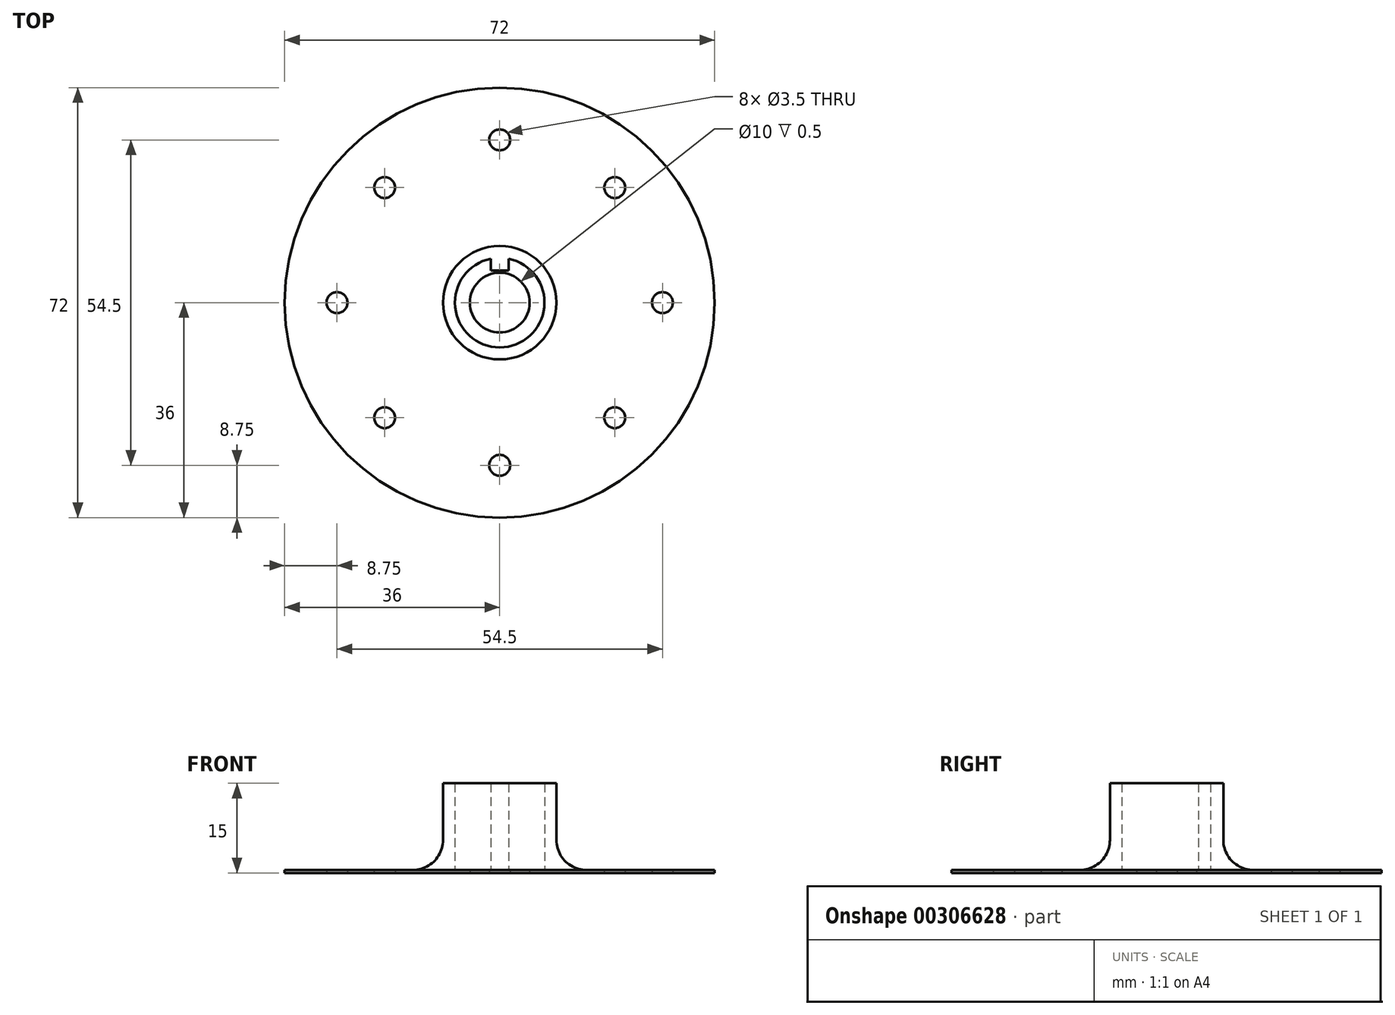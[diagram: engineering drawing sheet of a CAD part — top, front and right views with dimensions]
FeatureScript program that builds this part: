
annotation { "Feature Type Name" : "Feature", "Feature Type Description" : "" }
export const myFeature = defineFeature(function(context is Context, id is Id, definition is map)
    precondition{}
    {
        {
            assignVariable(context, id + "F0", {"name" : "Thicc", "anyValue" : .5});
        }
        {
            var Q0;
            Q0=qCreatedBy(makeId("Top.planeOp"),FACE);
            var sketch = newSketch(context, id + "F1", { "sketchPlane" : qUnion([Q0])});
            skCircle(sketch, "E0", {"center": v(0, 0) * mm, "radius": 7.5 * mm});
            skCircle(sketch, "E1", {"center": v(0, 0) * mm, "radius": 9.5 * mm});
            skLineSegment(sketch, "E2", {"start": v(-1.5, 7.35) * mm, "end": v(-1.5, 5.35) * mm});
            skLineSegment(sketch, "E3", {"start": v(-1.5, 5.35) * mm, "end": v(1.5, 5.35) * mm});
            skLineSegment(sketch, "E4", {"start": v(1.5, 5.35) * mm, "end": v(1.5, 7.35) * mm});
            skPoint(sketch, "E5", {"position": v(0, 5.35) * mm});
            skSolve(sketch);
        }
        {
            var Q0;
            Q0=qCreatedBy(makeId("Top.planeOp"),FACE);
            var sketch = newSketch(context, id + "F2", { "sketchPlane" : qUnion([Q0])});
            skCircle(sketch, "E6", {"center": v(0, 0) * mm, "radius": 2.5 * mm});
            skCircle(sketch, "E7", {"center": v(0, 0) * mm, "radius": 27.25 * mm});
            skCircle(sketch, "E8", {"center": v(0, 0) * mm, "radius": 6 * mm});
            skCircle(sketch, "E9", {"center": v(0, 0) * mm, "radius": 36 * mm});
            skPoint(sketch, "E10", {"position": v(-6, 0) * mm});
            skPoint(sketch, "E11", {"position": v(0, 6) * mm});
            skPoint(sketch, "E12", {"position": v(6, 0) * mm});
            skPoint(sketch, "E13", {"position": v(0, -6) * mm});
            skCircle(sketch, "E14", {"center": v(0, 0) * mm, "radius": 4 * mm, "construction": true});
            skCircle(sketch, "E15", {"center": v(0, 27.25) * mm, "radius": 1.75 * mm});
            skCircle(sketch, "E16.1.0", {"center": v(-19.27, 19.27) * mm, "radius": 1.75 * mm});
            skCircle(sketch, "E16.2.0", {"center": v(-27.25, 0) * mm, "radius": 1.75 * mm});
            skCircle(sketch, "E16.3.0", {"center": v(-19.27, -19.27) * mm, "radius": 1.75 * mm});
            skCircle(sketch, "E16.4.0", {"center": v(0, -27.25) * mm, "radius": 1.75 * mm});
            skCircle(sketch, "E16.5.0", {"center": v(19.27, -19.27) * mm, "radius": 1.75 * mm});
            skCircle(sketch, "E16.6.0", {"center": v(27.25, 0) * mm, "radius": 1.75 * mm});
            skCircle(sketch, "E16.7.0", {"center": v(19.27, 19.27) * mm, "radius": 1.75 * mm});
            skSolve(sketch);
        }
        {
            var Q0;
            Q0=makeQuery(id+"F2.imprint","IMPRINT",FACE,{"disambiguationData":[TD([[makeQuery(id+"F2.imprint","IMPRINT",EDGE,{"derivedFrom":sQuery(id+"F2.wireOp",EDGE,"E9")}),1.0]])]});
            var Q1;
            {var subQ9=sQuery(id+"F2.wireOp",EDGE,"dmMNSs5U-dXkE-OnuB-x4GF-gnbwgTEUMQlt");Q1=makeQuery(id+"F2.imprint","IMPRINT",FACE,{"disambiguationData":[TD([[makeQuery(id+"F2.imprint","IMPRINT",EDGE,{"derivedFrom":subQ9}),-1.0]])]});}
            var Q2;
            Q2=makeQuery(id+"F2.imprint","IMPRINT",FACE,{"disambiguationData":[TD([[makeQuery(id+"F2.imprint","IMPRINT",EDGE,{"derivedFrom":sQuery(id+"F2.wireOp",EDGE,"E6")}),-1.0]])]});
            var Q3;
            Q3=makeQuery(id+"F2.imprint","IMPRINT",FACE,{"disambiguationData":[TD([[makeQuery(id+"F2.imprint","IMPRINT",EDGE,{"derivedFrom":sQuery(id+"F2.wireOp",EDGE,"IWH39UaP-91kU-eHGR-F86Z-JhOdxDluEBEP")}),1.0]])]});
            var Q4;
            Q4=makeQuery(id+"F2.imprint","IMPRINT",FACE,{"disambiguationData":[TD([[makeQuery(id+"F2.imprint","IMPRINT",EDGE,{"derivedFrom":sQuery(id+"F2.wireOp",EDGE,"xcFHTZrV-l3IJ-FcGW-Rsgo-3uNkYJn71cBD")}),1.0]])]});
            var Q5;
            Q5=makeQuery(id+"F2.imprint","IMPRINT",FACE,{"disambiguationData":[TD([[makeQuery(id+"F2.imprint","IMPRINT",EDGE,{"derivedFrom":sQuery(id+"F2.wireOp",EDGE,"dmMNSs5U-dXkE-OnuB-x4GF-gnbwgTEUMQlt")}),1.0]])]});
            var Q6;
            Q6=makeQuery(id+"F2.imprint","IMPRINT",FACE,{"disambiguationData":[TD([[makeQuery(id+"F2.imprint","IMPRINT",EDGE,{"derivedFrom":sQuery(id+"F2.wireOp",EDGE,"OsnEyq0h-FFfx-xI0f-fycZ-s3bM1W6ctmpb")}),1.0]])]});
            var Q7;
            {var subQ0=sQuery(id+"F2.wireOp",EDGE,"W7DDKYX3-tOsd-kb3P-etkb-bdxIaiogGMYC");var subQ1=sQuery(id+"F2.wireOp",EDGE,"E7");var subQ2=makeQuery(id+"F2.imprint","INTERSECT",VERTEX,{"disambiguationData":[OD(0.0)],"derivedFrom":[subQ1,subQ0]});Q7=makeQuery(id+"F2.imprint","IMPRINT",FACE,{"disambiguationData":[TD([[makeQuery(id+"F2.imprint","IMPRINT",EDGE,{"disambiguationData":[TD([[subQ2,-1.0]])],"derivedFrom":subQ1}),-1.0]])]});}
            var Q8;
            {var subQ0=sQuery(id+"F2.wireOp",EDGE,"W7DDKYX3-tOsd-kb3P-etkb-bdxIaiogGMYC");var subQ1=sQuery(id+"F2.wireOp",EDGE,"E7");var subQ2=makeQuery(id+"F2.imprint","INTERSECT",VERTEX,{"disambiguationData":[OD(0.0)],"derivedFrom":[subQ1,subQ0]});Q8=makeQuery(id+"F2.imprint","IMPRINT",FACE,{"disambiguationData":[TD([[makeQuery(id+"F2.imprint","IMPRINT",EDGE,{"disambiguationData":[TD([[subQ2,-1.0]])],"derivedFrom":subQ1}),1.0]])]});}
            var Q9;
            {var subQ0=sQuery(id+"F2.wireOp",EDGE,"AhLqCoLq-dUsO-Cpqc-C8LF-fpEpIzBaevSX");var subQ1=sQuery(id+"F2.wireOp",EDGE,"E7");var subQ2=makeQuery(id+"F2.imprint","INTERSECT",VERTEX,{"disambiguationData":[OD(0.0)],"derivedFrom":[subQ1,subQ0]});Q9=makeQuery(id+"F2.imprint","IMPRINT",FACE,{"disambiguationData":[TD([[makeQuery(id+"F2.imprint","IMPRINT",EDGE,{"disambiguationData":[TD([[subQ2,-1.0]])],"derivedFrom":subQ1}),-1.0]])]});}
            var Q10;
            {var subQ0=sQuery(id+"F2.wireOp",EDGE,"AhLqCoLq-dUsO-Cpqc-C8LF-fpEpIzBaevSX");var subQ1=sQuery(id+"F2.wireOp",EDGE,"E7");var subQ2=makeQuery(id+"F2.imprint","INTERSECT",VERTEX,{"disambiguationData":[OD(0.0)],"derivedFrom":[subQ1,subQ0]});Q10=makeQuery(id+"F2.imprint","IMPRINT",FACE,{"disambiguationData":[TD([[makeQuery(id+"F2.imprint","IMPRINT",EDGE,{"disambiguationData":[TD([[subQ2,-1.0]])],"derivedFrom":subQ1}),1.0]])]});}
            var Q11;
            {var subQ0=sQuery(id+"F2.wireOp",EDGE,"NGUcrRit-ETaF-dVqX-X14s-6RHGiHHLhfyM");var subQ1=sQuery(id+"F2.wireOp",EDGE,"E7");var subQ2=makeQuery(id+"F2.imprint","INTERSECT",VERTEX,{"disambiguationData":[OD(0.0)],"derivedFrom":[subQ1,subQ0]});Q11=makeQuery(id+"F2.imprint","IMPRINT",FACE,{"disambiguationData":[TD([[makeQuery(id+"F2.imprint","IMPRINT",EDGE,{"disambiguationData":[TD([[subQ2,-1.0]])],"derivedFrom":subQ1}),1.0]])]});}
            var Q12;
            {var subQ0=sQuery(id+"F2.wireOp",EDGE,"NGUcrRit-ETaF-dVqX-X14s-6RHGiHHLhfyM");var subQ1=sQuery(id+"F2.wireOp",EDGE,"E7");var subQ2=makeQuery(id+"F2.imprint","INTERSECT",VERTEX,{"disambiguationData":[OD(0.0)],"derivedFrom":[subQ1,subQ0]});Q12=makeQuery(id+"F2.imprint","IMPRINT",FACE,{"disambiguationData":[TD([[makeQuery(id+"F2.imprint","IMPRINT",EDGE,{"disambiguationData":[TD([[subQ2,-1.0]])],"derivedFrom":subQ1}),-1.0]])]});}
            var Q13;
            {var subQ0=sQuery(id+"F2.wireOp",EDGE,"sCoCbA2o-mAqV-ztxx-V3PG-5PHjPGKNcyER");var subQ1=sQuery(id+"F2.wireOp",EDGE,"E7");var subQ2=makeQuery(id+"F2.imprint","INTERSECT",VERTEX,{"disambiguationData":[OD(0.0)],"derivedFrom":[subQ1,subQ0]});Q13=makeQuery(id+"F2.imprint","IMPRINT",FACE,{"disambiguationData":[TD([[makeQuery(id+"F2.imprint","IMPRINT",EDGE,{"disambiguationData":[TD([[subQ2,-1.0]])],"derivedFrom":subQ1}),-1.0]])]});}
            var Q14;
            {var subQ0=sQuery(id+"F2.wireOp",EDGE,"sCoCbA2o-mAqV-ztxx-V3PG-5PHjPGKNcyER");var subQ1=sQuery(id+"F2.wireOp",EDGE,"E7");var subQ2=makeQuery(id+"F2.imprint","INTERSECT",VERTEX,{"disambiguationData":[OD(0.0)],"derivedFrom":[subQ1,subQ0]});Q14=makeQuery(id+"F2.imprint","IMPRINT",FACE,{"disambiguationData":[TD([[makeQuery(id+"F2.imprint","IMPRINT",EDGE,{"disambiguationData":[TD([[subQ2,-1.0]])],"derivedFrom":subQ1}),1.0]])]});}
            var Q15;
            {var subQ0=sQuery(id+"F2.wireOp",EDGE,"Wlw0vmTn-JX6U-yLGY-ctTl-H7deExxbmCa6");var subQ1=sQuery(id+"F2.wireOp",EDGE,"E7");var subQ2=makeQuery(id+"F2.imprint","INTERSECT",VERTEX,{"disambiguationData":[OD(0.0)],"derivedFrom":[subQ1,subQ0]});Q15=makeQuery(id+"F2.imprint","IMPRINT",FACE,{"disambiguationData":[TD([[makeQuery(id+"F2.imprint","IMPRINT",EDGE,{"disambiguationData":[TD([[subQ2,-1.0]])],"derivedFrom":subQ1}),-1.0]])]});}
            var Q16;
            {var subQ0=sQuery(id+"F2.wireOp",EDGE,"Wlw0vmTn-JX6U-yLGY-ctTl-H7deExxbmCa6");var subQ1=sQuery(id+"F2.wireOp",EDGE,"E7");var subQ2=makeQuery(id+"F2.imprint","INTERSECT",VERTEX,{"disambiguationData":[OD(0.0)],"derivedFrom":[subQ1,subQ0]});Q16=makeQuery(id+"F2.imprint","IMPRINT",FACE,{"disambiguationData":[TD([[makeQuery(id+"F2.imprint","IMPRINT",EDGE,{"disambiguationData":[TD([[subQ2,-1.0]])],"derivedFrom":subQ1}),1.0]])]});}
            var Q17;
            {var subQ0=sQuery(id+"F2.wireOp",EDGE,"8RowS32Q-1VLD-2CXS-3MN8-J7dKdJTsdKHX");var subQ1=sQuery(id+"F2.wireOp",EDGE,"E7");var subQ2=makeQuery(id+"F2.imprint","INTERSECT",VERTEX,{"disambiguationData":[OD(0.0)],"derivedFrom":[subQ1,subQ0]});Q17=makeQuery(id+"F2.imprint","IMPRINT",FACE,{"disambiguationData":[TD([[makeQuery(id+"F2.imprint","IMPRINT",EDGE,{"disambiguationData":[TD([[subQ2,-1.0]])],"derivedFrom":subQ1}),-1.0]])]});}
            var Q18;
            {var subQ0=sQuery(id+"F2.wireOp",EDGE,"8RowS32Q-1VLD-2CXS-3MN8-J7dKdJTsdKHX");var subQ1=sQuery(id+"F2.wireOp",EDGE,"E7");var subQ2=makeQuery(id+"F2.imprint","INTERSECT",VERTEX,{"disambiguationData":[OD(0.0)],"derivedFrom":[subQ1,subQ0]});Q18=makeQuery(id+"F2.imprint","IMPRINT",FACE,{"disambiguationData":[TD([[makeQuery(id+"F2.imprint","IMPRINT",EDGE,{"disambiguationData":[TD([[subQ2,-1.0]])],"derivedFrom":subQ1}),1.0]])]});}
            var Q19;
            {var subQ0=sQuery(id+"F2.wireOp",EDGE,"zQOqT4qT-SfCx-kdpD-fXQS-ZJYawlyoc7iw");var subQ1=sQuery(id+"F2.wireOp",EDGE,"E7");var subQ2=makeQuery(id+"F2.imprint","INTERSECT",VERTEX,{"disambiguationData":[OD(0.0)],"derivedFrom":[subQ1,subQ0]});Q19=makeQuery(id+"F2.imprint","IMPRINT",FACE,{"disambiguationData":[TD([[makeQuery(id+"F2.imprint","IMPRINT",EDGE,{"disambiguationData":[TD([[subQ2,1.0]])],"derivedFrom":subQ1}),-1.0]])]});}
            var Q20;
            {var subQ0=sQuery(id+"F2.wireOp",EDGE,"zQOqT4qT-SfCx-kdpD-fXQS-ZJYawlyoc7iw");var subQ1=sQuery(id+"F2.wireOp",EDGE,"E7");var subQ2=makeQuery(id+"F2.imprint","INTERSECT",VERTEX,{"disambiguationData":[OD(0.0)],"derivedFrom":[subQ1,subQ0]});Q20=makeQuery(id+"F2.imprint","IMPRINT",FACE,{"disambiguationData":[TD([[makeQuery(id+"F2.imprint","IMPRINT",EDGE,{"disambiguationData":[TD([[subQ2,1.0]])],"derivedFrom":subQ1}),1.0]])]});}
            var Q21;
            {var subQ0=sQuery(id+"F2.wireOp",EDGE,"3rG95Ao5-sNqn-pAqd-HIEG-2JQ369jTarzZ");var subQ1=sQuery(id+"F2.wireOp",EDGE,"E7");var subQ2=makeQuery(id+"F2.imprint","INTERSECT",VERTEX,{"disambiguationData":[OD(0.0)],"derivedFrom":[subQ1,subQ0]});Q21=makeQuery(id+"F2.imprint","IMPRINT",FACE,{"disambiguationData":[TD([[makeQuery(id+"F2.imprint","IMPRINT",EDGE,{"disambiguationData":[TD([[subQ2,-1.0]])],"derivedFrom":subQ1}),-1.0]])]});}
            var Q22;
            {var subQ0=sQuery(id+"F2.wireOp",EDGE,"3rG95Ao5-sNqn-pAqd-HIEG-2JQ369jTarzZ");var subQ1=sQuery(id+"F2.wireOp",EDGE,"E7");var subQ2=makeQuery(id+"F2.imprint","INTERSECT",VERTEX,{"disambiguationData":[OD(0.0)],"derivedFrom":[subQ1,subQ0]});Q22=makeQuery(id+"F2.imprint","IMPRINT",FACE,{"disambiguationData":[TD([[makeQuery(id+"F2.imprint","IMPRINT",EDGE,{"disambiguationData":[TD([[subQ2,-1.0]])],"derivedFrom":subQ1}),1.0]])]});}
            var Q23;
            Q23=makeQuery(id+"F2.imprint","IMPRINT",FACE,{"disambiguationData":[TD([[makeQuery(id+"F2.imprint","IMPRINT",EDGE,{"derivedFrom":sQuery(id+"F2.wireOp",EDGE,"E8")}),-1.0]])]});
            extrude(context, id + "F3", {"entities" : qUnion([Q0, Q1, Q2, Q3, Q4, Q5, Q6, Q7, Q8, Q9, Q10, Q11, Q12, Q13, Q14, Q15, Q16, Q17, Q18, Q19, Q20, Q21, Q22, Q23]), "depth" : (getVariable(context, 'Thicc')) * mm});
        }
        {
            var Q0;
            Q0=makeQuery(id+"F1.imprint","IMPRINT",FACE,{"disambiguationData":[TD([[makeQuery(id+"F1.imprint","IMPRINT",EDGE,{"derivedFrom":sQuery(id+"F1.wireOp",EDGE,"E1")}),1.0]])]});
            var Q1;
            {var subQ0=sQuery(id+"F1.wireOp",EDGE,"E2");Q1=makeQuery(id+"F1.imprint","IMPRINT",FACE,{"disambiguationData":[TD([[makeQuery(id+"F1.imprint","IMPRINT",EDGE,{"derivedFrom":subQ0}),1.0]])]});}
            extrude(context, id + "F4", {"entities" : qUnion([Q0, Q1]), "operationType" : NewBodyOperationType.ADD, "depth" : 15 * mm});
        }
        {
            var Q0;
            Q0=makeQuery(id+"F4.boolean.opBoolean","INTERSECT",EDGE,{"derivedFrom":[makeQuery(id+"F3.opExtrude","CAP_FACE",FACE,{"disambiguationData":[OSD([sQuery(id+"F2.wireOp",EDGE,"E6"),sQuery(id+"F2.wireOp",EDGE,"E9"),sQuery(id+"F2.wireOp",EDGE,"sCoCbA2o-mAqV-ztxx-V3PG-5PHjPGKNcyER"),sQuery(id+"F2.wireOp",EDGE,"NGUcrRit-ETaF-dVqX-X14s-6RHGiHHLhfyM"),sQuery(id+"F2.wireOp",EDGE,"AhLqCoLq-dUsO-Cpqc-C8LF-fpEpIzBaevSX"),sQuery(id+"F2.wireOp",EDGE,"W7DDKYX3-tOsd-kb3P-etkb-bdxIaiogGMYC"),sQuery(id+"F2.wireOp",EDGE,"Wlw0vmTn-JX6U-yLGY-ctTl-H7deExxbmCa6"),sQuery(id+"F2.wireOp",EDGE,"8RowS32Q-1VLD-2CXS-3MN8-J7dKdJTsdKHX"),sQuery(id+"F2.wireOp",EDGE,"TLXLu7Ko-HqFY-d5sP-6ZKn-YTGZKyFlau6R"),sQuery(id+"F2.wireOp",EDGE,"3rG95Ao5-sNqn-pAqd-HIEG-2JQ369jTarzZ")])],"isStart":false}),makeQuery(id+"F4.opExtrude","SWEPT_FACE",FACE,{"disambiguationData":[OSD([sQuery(id+"F1.wireOp",EDGE,"E1")])]})]});
            fillet(context, id + "F5", {"entities" : qUnion([Q0]), "radius" : 5 * mm, "tangentPropagation" : true, "allowEdgeOverflow" : false});
        }
        {
            var Q0;
            Q0=sQuery(id+"F2.wireOp",VERTEX,"E9.center");
            var Q1;
            Q1=makeQuery(id+"F3.opExtrude","SWEPT_BODY",BODY,{"disambiguationData":[OSD([sQuery(id+"F2.wireOp",EDGE,"E6"),sQuery(id+"F2.wireOp",EDGE,"E9"),sQuery(id+"F2.wireOp",EDGE,"sCoCbA2o-mAqV-ztxx-V3PG-5PHjPGKNcyER"),sQuery(id+"F2.wireOp",EDGE,"NGUcrRit-ETaF-dVqX-X14s-6RHGiHHLhfyM"),sQuery(id+"F2.wireOp",EDGE,"AhLqCoLq-dUsO-Cpqc-C8LF-fpEpIzBaevSX"),sQuery(id+"F2.wireOp",EDGE,"W7DDKYX3-tOsd-kb3P-etkb-bdxIaiogGMYC"),sQuery(id+"F2.wireOp",EDGE,"Wlw0vmTn-JX6U-yLGY-ctTl-H7deExxbmCa6"),sQuery(id+"F2.wireOp",EDGE,"8RowS32Q-1VLD-2CXS-3MN8-J7dKdJTsdKHX"),sQuery(id+"F2.wireOp",EDGE,"TLXLu7Ko-HqFY-d5sP-6ZKn-YTGZKyFlau6R"),sQuery(id+"F2.wireOp",EDGE,"3rG95Ao5-sNqn-pAqd-HIEG-2JQ369jTarzZ")])]});
            hole(context, id + "F6", {"style" : HoleStyle.SIMPLE, "endStyle" : HoleEndStyle.BLIND, "oppositeDirection" : true, "holeDiameter" : 10 * mm, "holeDepth" : 3.5 * mm, "tappedDepth" : 12 * mm, "tapClearance" : 3, "startFromSketch" : true, "locations" : qUnion([Q0]), "scope" : qUnion([Q1])});
        }
    });
